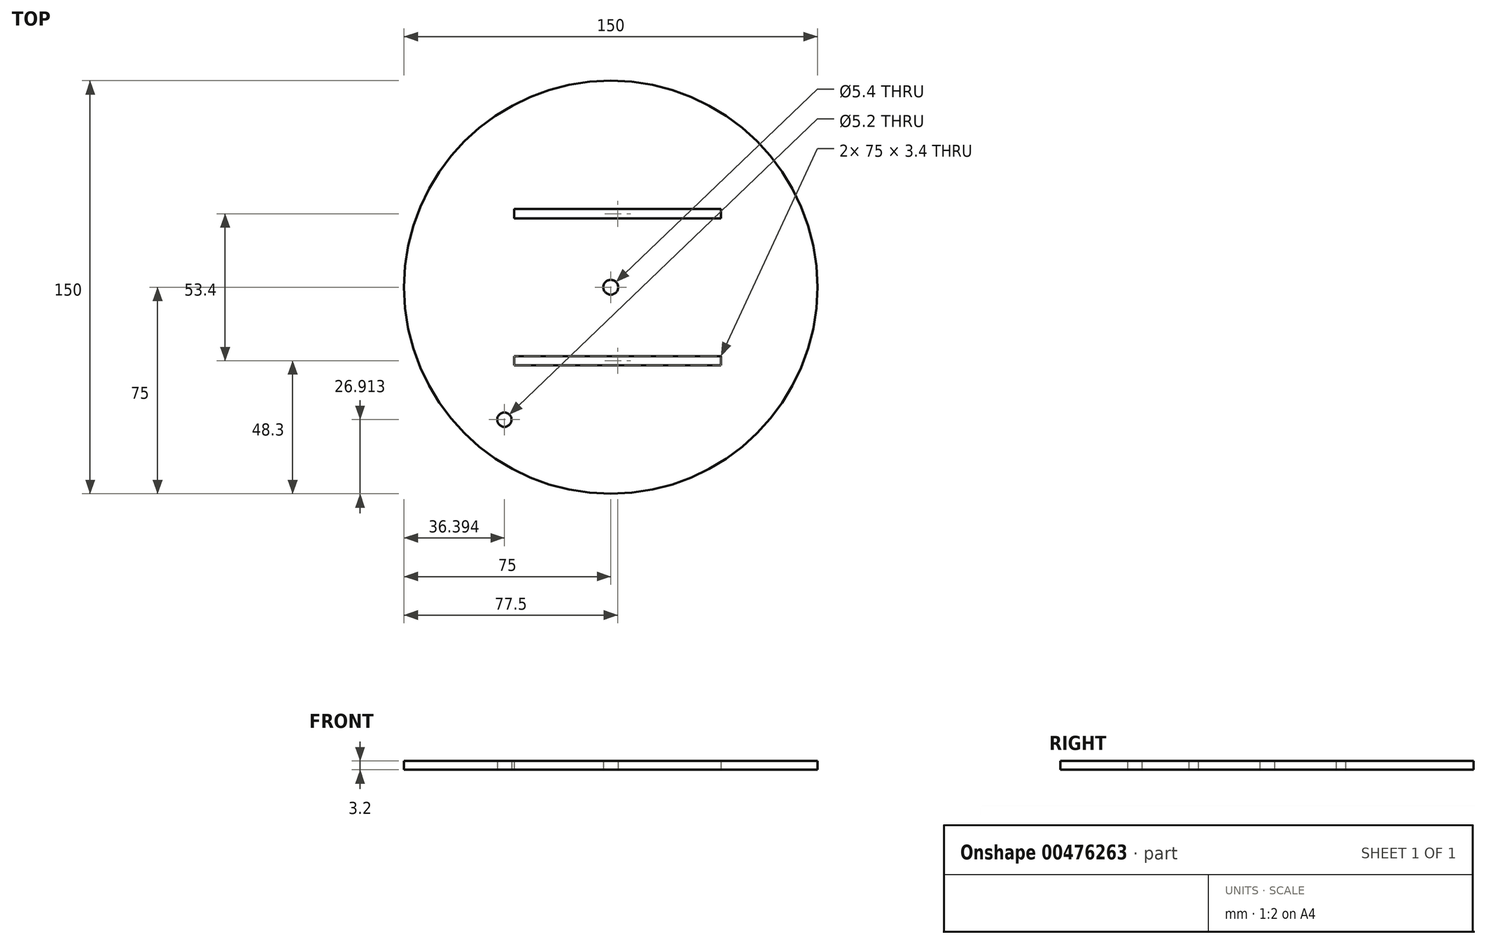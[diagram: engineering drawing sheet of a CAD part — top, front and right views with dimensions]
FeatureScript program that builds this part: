
annotation { "Feature Type Name" : "Feature", "Feature Type Description" : "" }
export const myFeature = defineFeature(function(context is Context, id is Id, definition is map)
    precondition{}
    {
        {
            var Q0;
            Q0=qCreatedBy(makeId("Top.planeOp"),FACE);
            var sketch = newSketch(context, id + "F0", { "sketchPlane" : qUnion([Q0])});
            skCircle(sketch, "E0", {"center": v(0, 0) * mm, "radius": 75 * mm});
            skLineSegment(sketch, "E1.bottom", {"start": v(-35, -25) * mm, "end": v(40, -25) * mm});
            skLineSegment(sketch, "E1.top", {"start": v(-35, -28.4) * mm, "end": v(40, -28.4) * mm});
            skLineSegment(sketch, "E1.left", {"start": v(-35, -25) * mm, "end": v(-35, -28.4) * mm});
            skLineSegment(sketch, "E1.right", {"start": v(40, -25) * mm, "end": v(40, -28.4) * mm});
            skCircle(sketch, "E2", {"center": v(0, 0) * mm, "radius": 2.7 * mm});
            skLineSegment(sketch, "E3.MirrorCS", {"start": v(-35, 25) * mm, "end": v(-35, 28.4) * mm});
            skLineSegment(sketch, "E4.MirrorCS", {"start": v(40, 25) * mm, "end": v(40, 28.4) * mm});
            skLineSegment(sketch, "E5.MirrorCS", {"start": v(-35, 25) * mm, "end": v(40, 25) * mm});
            skLineSegment(sketch, "E6.MirrorCS", {"start": v(-35, 28.4) * mm, "end": v(40, 28.4) * mm});
            skCircle(sketch, "E7", {"center": v(-38.6, -48.09) * mm, "radius": 2.6 * mm});
            skSolve(sketch);
        }
        {
            var Q0;
            Q0=makeQuery(id+"F0.imprint","IMPRINT",FACE,{"disambiguationData":[TD([[makeQuery(id+"F0.imprint","IMPRINT",EDGE,{"derivedFrom":sQuery(id+"F0.wireOp",EDGE,"E0")}),1.0]])]});
            extrude(context, id + "F1", {"entities" : qUnion([Q0]), "depth" : 3.2 * mm});
        }
    });
